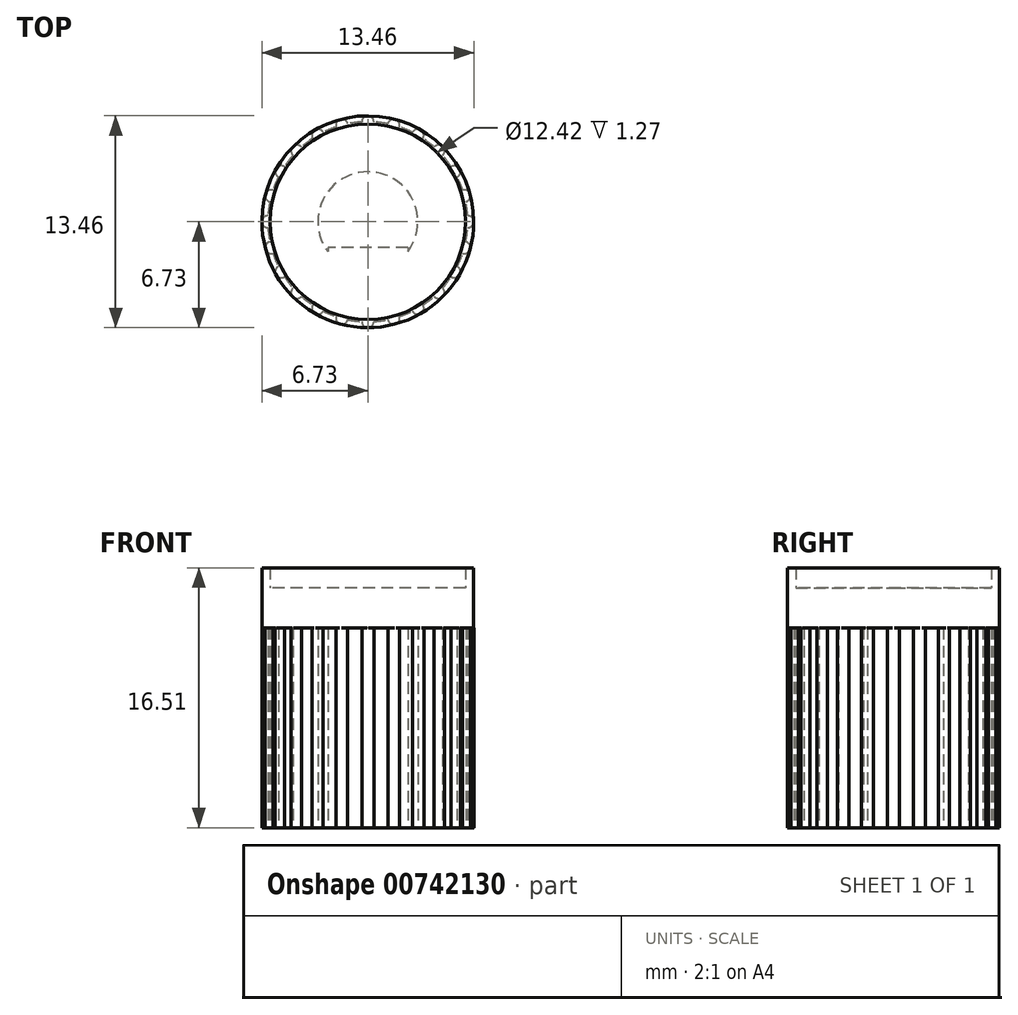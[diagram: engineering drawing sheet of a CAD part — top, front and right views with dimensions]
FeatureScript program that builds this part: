
annotation { "Feature Type Name" : "Feature", "Feature Type Description" : "" }
export const myFeature = defineFeature(function(context is Context, id is Id, definition is map)
    precondition{}
    {
        {
            var Q0;
            Q0=qCreatedBy(makeId("Top.planeOp"),FACE);
            var sketch = newSketch(context, id + "F0", { "sketchPlane" : qUnion([Q0])});
            skCircle(sketch, "E0", {"center": v(0, 0) * mm, "radius": 3.18 * mm});
            skCircle(sketch, "E1", {"center": v(0, 0) * mm, "radius": 6.35 * mm});
            skCircle(sketch, "E2", {"center": v(0, 6.35) * mm, "radius": 0.38 * mm});
            skCircle(sketch, "E3.1.0", {"center": v(-1.64, 6.13) * mm, "radius": 0.38 * mm});
            skCircle(sketch, "E3.2.0", {"center": v(-3.17, 5.5) * mm, "radius": 0.38 * mm});
            skCircle(sketch, "E3.3.0", {"center": v(-4.5, 4.5) * mm, "radius": 0.38 * mm});
            skCircle(sketch, "E3.4.0", {"center": v(-5.5, 3.18) * mm, "radius": 0.38 * mm});
            skCircle(sketch, "E3.5.0", {"center": v(-6.13, 1.64) * mm, "radius": 0.38 * mm});
            skCircle(sketch, "E3.6.0", {"center": v(-6.35, 0) * mm, "radius": 0.38 * mm});
            skCircle(sketch, "E3.7.0", {"center": v(-6.13, -1.64) * mm, "radius": 0.38 * mm});
            skCircle(sketch, "E3.8.0", {"center": v(-5.5, -3.17) * mm, "radius": 0.38 * mm});
            skCircle(sketch, "E3.9.0", {"center": v(-4.5, -4.5) * mm, "radius": 0.38 * mm});
            skCircle(sketch, "E3.10.0", {"center": v(-3.18, -5.5) * mm, "radius": 0.38 * mm});
            skCircle(sketch, "E3.11.0", {"center": v(-1.64, -6.13) * mm, "radius": 0.38 * mm});
            skCircle(sketch, "E3.12.0", {"center": v(0, -6.35) * mm, "radius": 0.38 * mm});
            skCircle(sketch, "E3.13.0", {"center": v(1.64, -6.13) * mm, "radius": 0.38 * mm});
            skCircle(sketch, "E3.14.0", {"center": v(3.17, -5.5) * mm, "radius": 0.38 * mm});
            skCircle(sketch, "E3.15.0", {"center": v(4.5, -4.5) * mm, "radius": 0.38 * mm});
            skCircle(sketch, "E3.16.0", {"center": v(5.5, -3.18) * mm, "radius": 0.38 * mm});
            skCircle(sketch, "E3.17.0", {"center": v(6.13, -1.64) * mm, "radius": 0.38 * mm});
            skCircle(sketch, "E3.18.0", {"center": v(6.35, 0) * mm, "radius": 0.38 * mm});
            skCircle(sketch, "E3.19.0", {"center": v(6.13, 1.64) * mm, "radius": 0.38 * mm});
            skCircle(sketch, "E3.20.0", {"center": v(5.5, 3.17) * mm, "radius": 0.38 * mm});
            skCircle(sketch, "E3.21.0", {"center": v(4.5, 4.5) * mm, "radius": 0.38 * mm});
            skCircle(sketch, "E3.22.0", {"center": v(3.18, 5.5) * mm, "radius": 0.38 * mm});
            skCircle(sketch, "E3.23.0", {"center": v(1.64, 6.13) * mm, "radius": 0.38 * mm});
            skSolve(sketch);
        }
        {
            var Q0;
            Q0=qCreatedBy(makeId("Top.planeOp"),FACE);
            var sketch = newSketch(context, id + "F1", { "sketchPlane" : qUnion([Q0])});
            skLineSegment(sketch, "E4.bottom", {"start": v(2.54, -1.65) * mm, "end": v(-2.54, -1.65) * mm});
            skLineSegment(sketch, "E4.top", {"start": v(2.54, -3.68) * mm, "end": v(-2.54, -3.68) * mm});
            skLineSegment(sketch, "E4.left", {"start": v(2.54, -1.65) * mm, "end": v(2.54, -3.68) * mm});
            skLineSegment(sketch, "E4.right", {"start": v(-2.54, -1.65) * mm, "end": v(-2.54, -3.68) * mm});
            skPoint(sketch, "E4.middle", {"position": v(0, -2.67) * mm});
            skSolve(sketch);
        }
        {
            var Q0;
            Q0=qSketchRegion(id+"F0",true);
            extrude(context, id + "F2", {"entities" : qUnion([Q0]), "depth" : 12.7 * mm, "offsetDistance" : 25.4 * mm});
        }
        {
            var Q0;
            Q0=qSketchRegion(id+"F1",true);
            extrude(context, id + "F3", {"entities" : qUnion([Q0]), "operationType" : NewBodyOperationType.ADD, "depth" : 12.7 * mm, "offsetDistance" : 25.4 * mm});
        }
        {
            var Q0;
            Q0=qCreatedBy(makeId("Top.planeOp"),FACE);
            cPlane(context, id + "F4", {"entities" : qUnion([Q0]), "cplaneType" : CPlaneType.OFFSET, "offset" : 12.7 * mm, "width" : 152.4 * mm, "height" : 152.4 * mm});
        }
        {
            var Q0;
            Q0=qCreatedBy(id+"F4.planeOp",FACE);
            var sketch = newSketch(context, id + "F5", { "sketchPlane" : qUnion([Q0])});
            skCircle(sketch, "E5", {"center": v(0, 0) * mm, "radius": 5.08 * mm});
            skCircle(sketch, "E6", {"center": v(0, 0) * mm, "radius": 6.73 * mm});
            skCircle(sketch, "E7", {"center": v(0, 0) * mm, "radius": 6.2 * mm});
            skSolve(sketch);
        }
        {
            var Q0;
            Q0=makeQuery(id+"F5.imprint","IMPRINT",FACE,{"disambiguationData":[TD([[makeQuery(id+"F5.imprint","IMPRINT",EDGE,{"derivedFrom":sQuery(id+"F5.wireOp",EDGE,"E6")}),1.0]])]});
            extrude(context, id + "F6", {"entities" : qUnion([Q0]), "operationType" : NewBodyOperationType.ADD, "depth" : 3.8 * mm, "offsetDistance" : 25.4 * mm});
        }
        {
            var Q0;
            Q0=qCreatedBy(id+"F4.planeOp",FACE);
            var sketch = newSketch(context, id + "F7", { "sketchPlane" : qUnion([Q0])});
            skCircle(sketch, "E8", {"center": v(0, 0) * mm, "radius": 6.29 * mm});
            skSolve(sketch);
        }
        {
            var Q0;
            Q0 = qSketchRegion(id + "F7", true);
            extrude(context, id + "F8", {"entities" : qUnion([Q0]), "operationType" : NewBodyOperationType.ADD, "depth" : 2.54 * mm, "offsetDistance" : 25.4 * mm});
        }
    });
